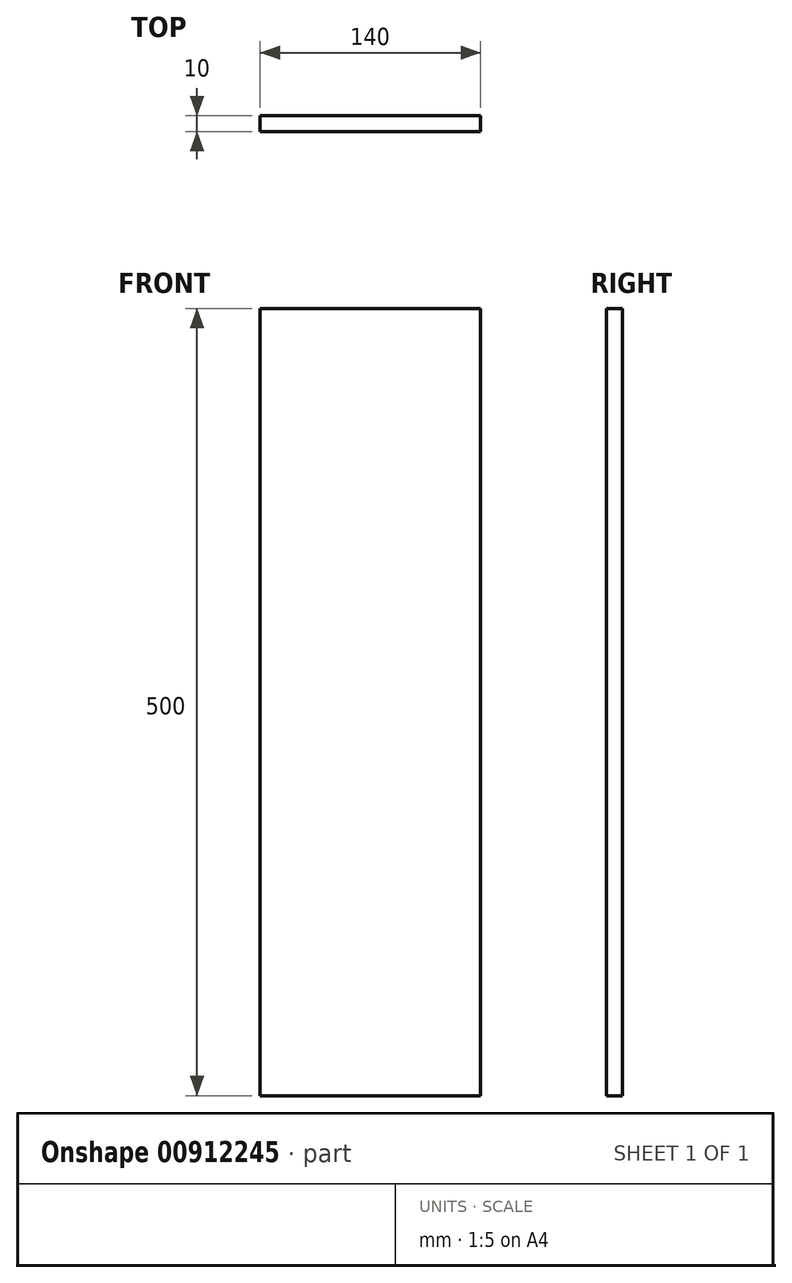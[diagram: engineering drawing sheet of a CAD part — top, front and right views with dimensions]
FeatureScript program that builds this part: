
annotation { "Feature Type Name" : "Feature", "Feature Type Description" : "" }
export const myFeature = defineFeature(function(context is Context, id is Id, definition is map)
    precondition{}
    {
        {
            var Q0;
            Q0=qCreatedBy(makeId("Front.planeOp"),FACE);
            var sketch = newSketch(context, id + "F0", { "sketchPlane" : qUnion([Q0])});
            skLineSegment(sketch, "E0.bottom", {"start": v(-68.95, 461.68) * mm, "end": v(71.05, 461.68) * mm});
            skLineSegment(sketch, "E0.top", {"start": v(-68.95, -38.32) * mm, "end": v(71.05, -38.32) * mm});
            skLineSegment(sketch, "E0.left", {"start": v(-68.95, 461.68) * mm, "end": v(-68.95, -38.32) * mm});
            skLineSegment(sketch, "E0.right", {"start": v(71.05, 461.68) * mm, "end": v(71.05, -38.32) * mm});
            skSolve(sketch);
        }
        {
            var Q0;
            Q0=makeQuery(id+"F0.imprint","IMPRINT",FACE,{"disambiguationData":[TD([[makeQuery(id+"F0.imprint","IMPRINT",EDGE,{"derivedFrom":sQuery(id+"F0.wireOp",EDGE,"E0.bottom")}),-1.0]])]});
            extrude(context, id + "F1", {"entities" : qUnion([Q0]), "depth" : 10 * mm, "offsetDistance" : 25 * mm});
        }
    });
